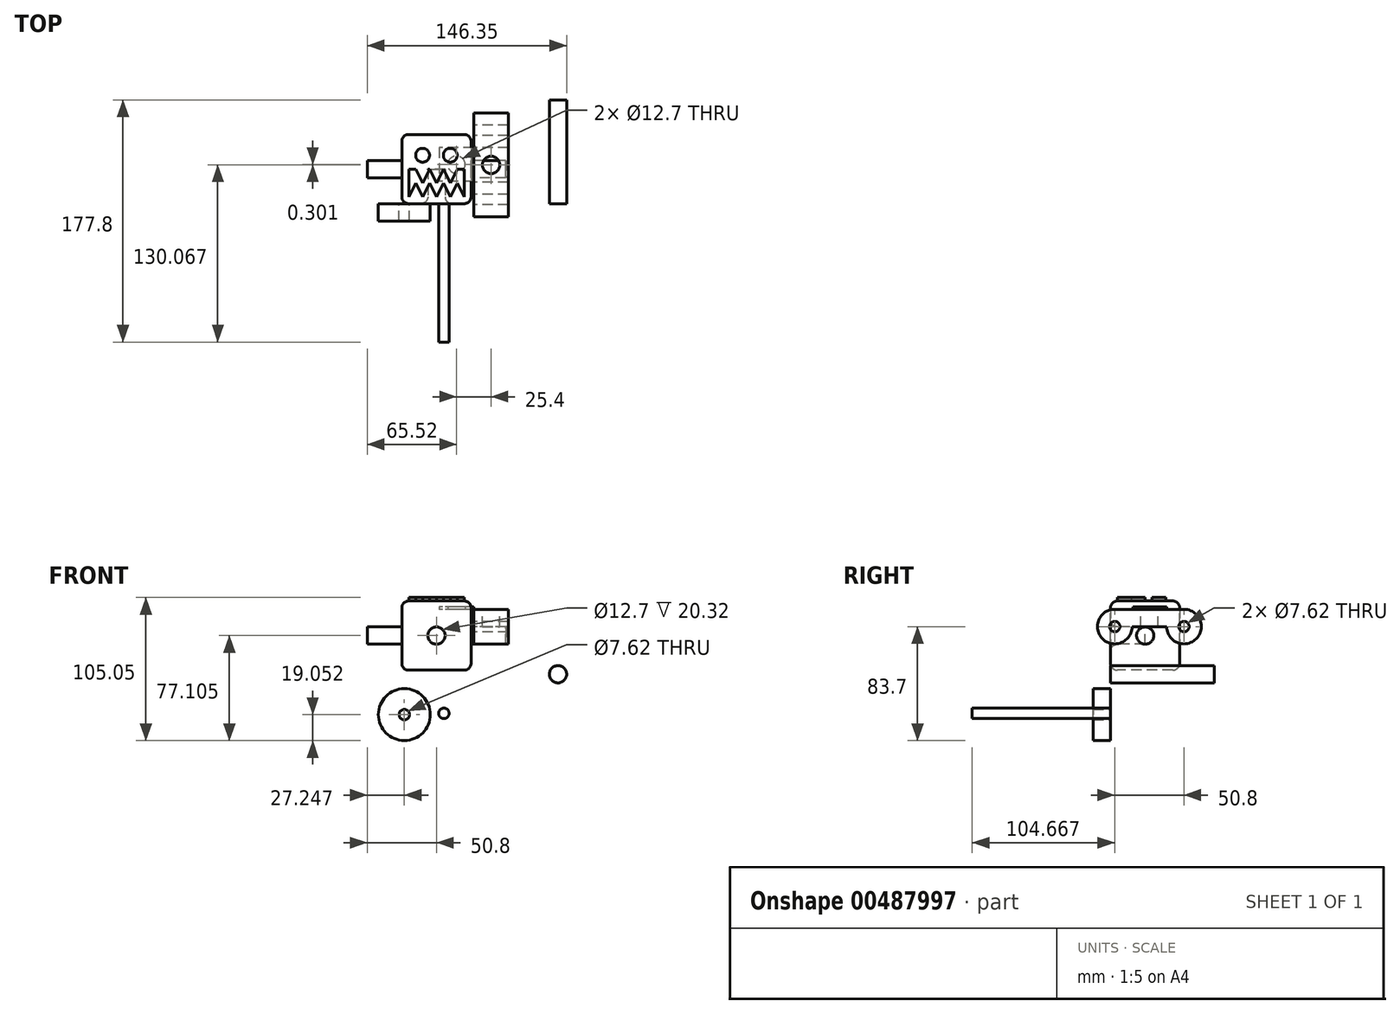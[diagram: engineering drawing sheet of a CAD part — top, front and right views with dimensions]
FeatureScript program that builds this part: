
annotation { "Feature Type Name" : "Feature", "Feature Type Description" : "" }
export const myFeature = defineFeature(function(context is Context, id is Id, definition is map)
    precondition{}
    {
        {
            var Q0;
            Q0=qCreatedBy(makeId("Front.planeOp"),FACE);
            var sketch = newSketch(context, id + "F0", { "sketchPlane" : qUnion([Q0])});
            skCircle(sketch, "E0", {"center": v(-50.97, -29.67) * mm, "radius": 19.05 * mm});
            skCircle(sketch, "E1", {"center": v(-50.97, -29.67) * mm, "radius": 3.81 * mm});
            skSolve(sketch);
        }
        {
            var Q0;
            Q0 = qSketchRegion(id + "F0", true);
            extrude(context, id + "F1", {"entities" : qUnion([Q0]), "depth" : 12.7 * mm, "offsetDistance" : 25.4 * mm});
        }
        {
            var Q0;
            Q0=qCreatedBy(makeId("Front.planeOp"),FACE);
            var sketch = newSketch(context, id + "F2", { "sketchPlane" : qUnion([Q0])});
            skCircle(sketch, "E2", {"center": v(-21.94, -28.72) * mm, "radius": 3.81 * mm});
            skSolve(sketch);
        }
        {
            var Q0;
            Q0 = qSketchRegion(id + "F2", true);
            extrude(context, id + "F3", {"entities" : qUnion([Q0]), "depth" : 101.6 * mm, "offsetDistance" : 25.4 * mm});
        }
        {
            var Q0;
            Q0=qCreatedBy(makeId("Right.planeOp"),FACE);
            var sketch = newSketch(context, id + "F4", { "sketchPlane" : qUnion([Q0])});
            skCircle(sketch, "E3", {"center": v(53.87, 34.98) * mm, "radius": 12.7 * mm});
            skCircle(sketch, "E4", {"center": v(53.87, 34.98) * mm, "radius": 3.81 * mm});
            skLineSegment(sketch, "E5", {"start": v(41.17, 34.98) * mm, "end": v(15.77, 34.98) * mm});
            skCircle(sketch, "E6", {"center": v(3.07, 34.98) * mm, "radius": 12.7 * mm});
            skCircle(sketch, "E7", {"center": v(3.07, 34.98) * mm, "radius": 3.81 * mm});
            skLineSegment(sketch, "E8", {"start": v(53.87, 47.68) * mm, "end": v(3.07, 47.68) * mm});
            skLineSegment(sketch, "E9", {"start": v(53.87, 22.28) * mm, "end": v(3.07, 22.28) * mm});
            skSolve(sketch);
        }
        {
            var Q0;
            Q0=makeQuery(id+"F4.imprint","IMPRINT",FACE,{"disambiguationData":[TD([[makeQuery(id+"F4.imprint","IMPRINT",EDGE,{"derivedFrom":sQuery(id+"F4.wireOp",EDGE,"E4")}),-1.0]])]});
            var Q1;
            Q1=makeQuery(id+"F4.imprint","IMPRINT",FACE,{"disambiguationData":[TD([[makeQuery(id+"F4.imprint","IMPRINT",EDGE,{"derivedFrom":sQuery(id+"F4.wireOp",EDGE,"E7")}),-1.0]])]});
            var Q2;
            {var subQ0=sQuery(id+"F4.wireOp",EDGE,"E5");Q2=makeQuery(id+"F4.imprint","IMPRINT",FACE,{"disambiguationData":[TD([[makeQuery(id+"F4.imprint","IMPRINT",EDGE,{"derivedFrom":subQ0}),-1.0]])]});}
            extrude(context, id + "F5", {"entities" : qUnion([Q0, Q1, Q2]), "depth" : 25.4 * mm, "offsetDistance" : 25.4 * mm});
        }
        {
            var Q0;
            Q0=makeQuery(id+"F5.opExtrude","SWEPT_FACE",FACE,{"disambiguationData":[OSD([sQuery(id+"F4.wireOp",EDGE,"E8")])]});
            var sketch = newSketch(context, id + "F6", { "sketchPlane" : qUnion([Q0])});
            skCircle(sketch, "E10", {"center": v(12.7, 28.47) * mm, "radius": 6.35 * mm});
            skPoint(sketch, "E10.centerSnap0", {"position": v(0, 28.47) * mm});
            skPoint(sketch, "E10.centerSnap1", {"position": v(12.7, 53.87) * mm});
            skSolve(sketch);
        }
        {
            var Q0;
            Q0 = qSketchRegion(id + "F6", true);
            extrude(context, id + "F7", {"entities" : qUnion([Q0]), "operationType" : NewBodyOperationType.REMOVE, "endBound" : BoundingType.THROUGH_ALL, "oppositeDirection" : true, "depth" : 25.4 * mm, "offsetDistance" : 25.4 * mm});
        }
        {
            var Q0;
            Q0=qCreatedBy(makeId("Top.planeOp"),FACE);
            var sketch = newSketch(context, id + "F8", { "sketchPlane" : qUnion([Q0])});
            skLineSegment(sketch, "E11", {"start": v(68.13, 76.2) * mm, "end": v(68.13, 0) * mm});
            skLineSegment(sketch, "E12", {"start": v(68.13, 76.2) * mm, "end": v(61.78, 76.2) * mm});
            skLineSegment(sketch, "E13", {"start": v(61.78, 76.2) * mm, "end": v(61.78, 0) * mm});
            skLineSegment(sketch, "E14", {"start": v(68.13, 0) * mm, "end": v(61.78, 0) * mm});
            skSolve(sketch);
        }
        {
            var Q0;
            Q0=makeQuery(id+"F8.imprint","IMPRINT",FACE,{"disambiguationData":[TD([[makeQuery(id+"F8.imprint","IMPRINT",EDGE,{"derivedFrom":sQuery(id+"F8.wireOp",EDGE,"E11")}),-1.0]])]});
            var Q1;
            Q1=sQuery(id+"F8.wireOp",EDGE,"E13");
            revolve(context, id + "F9", {"surfaceOperationType" : NewSurfaceOperationType.NEW, "entities" : qUnion([Q0]), "axis" : qUnion([Q1]), "revolveType" : RevolveType.FULL});
        }
        {
            var Q0;
            Q0=makeQuery(id+"F5.opExtrude","SWEPT_FACE",FACE,{"disambiguationData":[OSD([sQuery(id+"F4.wireOp",EDGE,"E8")])]});
            var sketch = newSketch(context, id + "F10", { "sketchPlane" : qUnion([Q0])});
            skLineSegment(sketch, "E15", {"start": v(0, 41.2) * mm, "end": v(0, 16.34) * mm});
            skLineSegment(sketch, "E16.MirrorCS", {"start": v(0, 41.2) * mm, "end": v(-25.4, 41.2) * mm});
            skLineSegment(sketch, "E17.MirrorCS", {"start": v(-25.4, 41.2) * mm, "end": v(-25.4, 16.34) * mm});
            skLineSegment(sketch, "E18.MirrorCS", {"start": v(0, 16.34) * mm, "end": v(-25.4, 16.34) * mm});
            skCircle(sketch, "E19", {"center": v(-12.7, 28.77) * mm, "radius": 6.35 * mm});
            skSolve(sketch);
        }
        {
            var Q0;
            Q0=makeQuery(id+"F10.imprint","IMPRINT",FACE,{"disambiguationData":[TD([[makeQuery(id+"F10.imprint","IMPRINT",EDGE,{"derivedFrom":sQuery(id+"F10.wireOp",EDGE,"E16.MirrorCS")}),1.0]])]});
            extrude(context, id + "F11", {"entities" : qUnion([Q0]), "depth" : 1.9 * mm, "offsetDistance" : 25.4 * mm});
        }
        {
            var Q0;
            Q0=qCreatedBy(makeId("Front.planeOp"),FACE);
            var sketch = newSketch(context, id + "F12", { "sketchPlane" : qUnion([Q0])});
            skLineSegment(sketch, "E20", {"start": v(-52.82, 53.79) * mm, "end": v(-52.82, 2.99) * mm});
            skLineSegment(sketch, "E21", {"start": v(-52.82, 2.99) * mm, "end": v(-2.02, 2.99) * mm});
            skLineSegment(sketch, "E22", {"start": v(-2.02, 2.99) * mm, "end": v(-2.02, 53.79) * mm});
            skLineSegment(sketch, "E23", {"start": v(-2.02, 53.79) * mm, "end": v(-52.82, 53.79) * mm});
            skCircle(sketch, "E24", {"center": v(-27.42, 28.39) * mm, "radius": 6.35 * mm});
            skPoint(sketch, "E24.centerSnap0", {"position": v(-27.42, 53.79) * mm});
            skPoint(sketch, "E24.centerSnap1", {"position": v(-52.82, 28.39) * mm});
            skSolve(sketch);
        }
        {
            var Q0;
            Q0=makeQuery(id+"F12.imprint","IMPRINT",FACE,{"disambiguationData":[TD([[makeQuery(id+"F12.imprint","IMPRINT",EDGE,{"derivedFrom":sQuery(id+"F12.wireOp",EDGE,"E20")}),1.0]])]});
            var Q1;
            Q1=makeQuery(id+"F12.imprint","IMPRINT",FACE,{"disambiguationData":[TD([[makeQuery(id+"F12.imprint","IMPRINT",EDGE,{"derivedFrom":sQuery(id+"F12.wireOp",EDGE,"E24")}),1.0]])]});
            extrude(context, id + "F13", {"entities" : qUnion([Q0, Q1]), "oppositeDirection" : true, "depth" : 50.8 * mm, "offsetDistance" : 25.4 * mm});
        }
        {
            var Q0;
            Q0=makeQuery(id+"F13.opExtrude","CAP_FACE",FACE,{"disambiguationData":[OSD([sQuery(id+"F12.wireOp",EDGE,"E20"),sQuery(id+"F12.wireOp",EDGE,"E21"),sQuery(id+"F12.wireOp",EDGE,"E22"),sQuery(id+"F12.wireOp",EDGE,"E23")])],"isStart":true});
            var sketch = newSketch(context, id + "F14", { "sketchPlane" : qUnion([Q0])});
            skCircle(sketch, "E25", {"center": v(-27.42, 28.39) * mm, "radius": 6.35 * mm});
            skSolve(sketch);
        }
        {
            var Q0;
            Q0=makeQuery(id+"F14.imprint","IMPRINT",FACE,{"disambiguationData":[TD([[makeQuery(id+"F14.imprint","IMPRINT",EDGE,{"derivedFrom":sQuery(id+"F14.wireOp",EDGE,"E25")}),1.0]])]});
            extrude(context, id + "F15", {"entities" : qUnion([Q0]), "operationType" : NewBodyOperationType.REMOVE, "oppositeDirection" : true, "depth" : 25.4 * mm, "offsetDistance" : 25.4 * mm});
        }
        {
            var Q0;
            Q0=makeQuery(id+"F13.opExtrude","CAP_EDGE",EDGE,{"disambiguationData":[OSD([sQuery(id+"F12.wireOp",EDGE,"E23")])],"isStart":true});
            var Q1;
            Q1=makeQuery(id+"F13.opExtrude","SWEPT_EDGE",EDGE,{"disambiguationData":[OSD([sQuery(id+"F12.wireOp",EDGE,"E20"),sQuery(id+"F12.wireOp",EDGE,"E23")])]});
            var Q2;
            Q2=makeQuery(id+"F13.opExtrude","CAP_EDGE",EDGE,{"disambiguationData":[OSD([sQuery(id+"F12.wireOp",EDGE,"E20")])],"isStart":true});
            var Q3;
            Q3=makeQuery(id+"F13.opExtrude","SWEPT_EDGE",EDGE,{"disambiguationData":[OSD([sQuery(id+"F12.wireOp",EDGE,"E20"),sQuery(id+"F12.wireOp",EDGE,"E21")])]});
            var Q4;
            Q4=makeQuery(id+"F13.opExtrude","CAP_EDGE",EDGE,{"disambiguationData":[OSD([sQuery(id+"F12.wireOp",EDGE,"E21")])],"isStart":true});
            var Q5;
            Q5=makeQuery(id+"F13.opExtrude","CAP_FACE",FACE,{"disambiguationData":[OSD([sQuery(id+"F12.wireOp",EDGE,"E20"),sQuery(id+"F12.wireOp",EDGE,"E21"),sQuery(id+"F12.wireOp",EDGE,"E22"),sQuery(id+"F12.wireOp",EDGE,"E23")])],"isStart":true});
            var Q6;
            Q6=makeQuery(id+"F13.opExtrude","SWEPT_EDGE",EDGE,{"disambiguationData":[OSD([sQuery(id+"F12.wireOp",EDGE,"E21"),sQuery(id+"F12.wireOp",EDGE,"E22")])]});
            var Q7;
            Q7=makeQuery(id+"F13.opExtrude","CAP_EDGE",EDGE,{"disambiguationData":[OSD([sQuery(id+"F12.wireOp",EDGE,"E23")])],"isStart":false});
            var Q8;
            Q8=makeQuery(id+"F13.opExtrude","SWEPT_EDGE",EDGE,{"disambiguationData":[OSD([sQuery(id+"F12.wireOp",EDGE,"E22"),sQuery(id+"F12.wireOp",EDGE,"E23")])]});
            var Q9;
            Q9=makeQuery(id+"F13.opExtrude","CAP_EDGE",EDGE,{"disambiguationData":[OSD([sQuery(id+"F12.wireOp",EDGE,"E22")])],"isStart":false});
            var Q10;
            Q10=makeQuery(id+"F13.opExtrude","CAP_EDGE",EDGE,{"disambiguationData":[OSD([sQuery(id+"F12.wireOp",EDGE,"E20")])],"isStart":false});
            var Q11;
            Q11=makeQuery(id+"F13.opExtrude","CAP_EDGE",EDGE,{"disambiguationData":[OSD([sQuery(id+"F12.wireOp",EDGE,"E21")])],"isStart":false});
            fillet(context, id + "F16", {"entities" : qUnion([Q0, Q1, Q2, Q3, Q4, Q5, Q6, Q7, Q8, Q9, Q10, Q11]), "radius" : 5.08 * mm, "tangentPropagation" : true, "allowEdgeOverflow" : false});
        }
        {
            var Q0;
            Q0=makeQuery(id+"F13.opExtrude","SWEPT_FACE",FACE,{"disambiguationData":[OSD([sQuery(id+"F12.wireOp",EDGE,"E20")])]});
            var sketch = newSketch(context, id + "F17", { "sketchPlane" : qUnion([Q0])});
            skCircle(sketch, "E26", {"center": v(-25.4, 28.39) * mm, "radius": 6.35 * mm});
            skPoint(sketch, "E26.centerSnap0", {"position": v(-5.08, 28.39) * mm});
            skPoint(sketch, "E26.centerSnap1", {"position": v(-25.4, 48.7) * mm});
            skSolve(sketch);
        }
        {
            var Q0;
            Q0=makeQuery(id+"F17.imprint","IMPRINT",FACE,{"disambiguationData":[TD([[makeQuery(id+"F17.imprint","IMPRINT",EDGE,{"derivedFrom":sQuery(id+"F17.wireOp",EDGE,"E26")}),1.0]])]});
            extrude(context, id + "F18", {"entities" : qUnion([Q0]), "operationType" : NewBodyOperationType.ADD, "depth" : 25.4 * mm, "offsetDistance" : 25.4 * mm});
        }
        {
            var Q0;
            Q0=makeQuery(id+"F13.opExtrude","SWEPT_FACE",FACE,{"disambiguationData":[OSD([sQuery(id+"F12.wireOp",EDGE,"E22")])]});
            var sketch = newSketch(context, id + "F19", { "sketchPlane" : qUnion([Q0])});
            skCircle(sketch, "E27", {"center": v(25.4, 28.39) * mm, "radius": 6.35 * mm});
            skPoint(sketch, "E27.centerSnap0", {"position": v(5.08, 28.39) * mm});
            skPoint(sketch, "E27.centerSnap1", {"position": v(25.4, 48.7) * mm});
            skSolve(sketch);
        }
        {
            var Q0;
            Q0 = qSketchRegion(id + "F19", true);
            extrude(context, id + "F20", {"entities" : qUnion([Q0]), "operationType" : NewBodyOperationType.ADD, "depth" : 25.4 * mm, "offsetDistance" : 25.4 * mm});
        }
        {
            var Q0;
            Q0=makeQuery(id+"F13.opExtrude","SWEPT_FACE",FACE,{"disambiguationData":[OSD([sQuery(id+"F12.wireOp",EDGE,"E23")])]});
            var sketch = newSketch(context, id + "F21", { "sketchPlane" : qUnion([Q0])});
            skCircle(sketch, "E28", {"center": v(-37.58, 35.56) * mm, "radius": 5.08 * mm});
            skCircle(sketch, "E29", {"center": v(-17.26, 35.56) * mm, "radius": 5.08 * mm});
            skLineSegment(sketch, "E30.left", {"start": v(-47.74, 25.4) * mm, "end": v(-47.74, 5.08) * mm});
            skLineSegment(sketch, "E30.right", {"start": v(-7.1, 25.4) * mm, "end": v(-7.1, 5.08) * mm});
            skLineSegment(sketch, "E31", {"start": v(-47.74, 5.08) * mm, "end": v(-37.58, 5.08) * mm});
            skLineSegment(sketch, "E32", {"start": v(-42.66, 15.24) * mm, "end": v(-47.74, 5.08) * mm});
            skLineSegment(sketch, "E33", {"start": v(-42.66, 15.24) * mm, "end": v(-37.58, 5.08) * mm});
            skLineSegment(sketch, "E34", {"start": v(-37.58, 5.08) * mm, "end": v(-32.5, 15.24) * mm});
            skLineSegment(sketch, "E35", {"start": v(-32.5, 15.24) * mm, "end": v(-27.42, 5.08) * mm});
            skLineSegment(sketch, "E36", {"start": v(-27.42, 5.08) * mm, "end": v(-22.34, 15.24) * mm});
            skLineSegment(sketch, "E37", {"start": v(-22.34, 15.24) * mm, "end": v(-17.26, 5.08) * mm});
            skLineSegment(sketch, "E38", {"start": v(-17.26, 5.08) * mm, "end": v(-12.18, 15.24) * mm});
            skLineSegment(sketch, "E39", {"start": v(-47.74, 25.4) * mm, "end": v(-37.58, 25.4) * mm});
            skLineSegment(sketch, "E40", {"start": v(-37.58, 25.4) * mm, "end": v(-27.42, 25.4) * mm});
            skLineSegment(sketch, "E41", {"start": v(-27.42, 25.4) * mm, "end": v(-17.26, 25.4) * mm});
            skLineSegment(sketch, "E42", {"start": v(-17.26, 25.4) * mm, "end": v(-7.1, 25.4) * mm});
            skLineSegment(sketch, "E43", {"start": v(-42.66, 25.4) * mm, "end": v(-37.58, 15.24) * mm});
            skLineSegment(sketch, "E44", {"start": v(-32.5, 25.4) * mm, "end": v(-37.58, 15.24) * mm});
            skLineSegment(sketch, "E45", {"start": v(-32.5, 25.4) * mm, "end": v(-27.42, 15.24) * mm});
            skLineSegment(sketch, "E46", {"start": v(-22.34, 25.4) * mm, "end": v(-27.42, 15.24) * mm});
            skLineSegment(sketch, "E47", {"start": v(-22.34, 25.4) * mm, "end": v(-17.26, 15.24) * mm});
            skLineSegment(sketch, "E48", {"start": v(-17.26, 15.24) * mm, "end": v(-12.18, 25.4) * mm});
            skLineSegment(sketch, "E49", {"start": v(-12.18, 15.24) * mm, "end": v(-7.1, 5.08) * mm});
            skSolve(sketch);
        }
        {
            var Q0;
            Q0=makeQuery(id+"F21.imprint","IMPRINT",FACE,{"disambiguationData":[TD([[makeQuery(id+"F21.imprint","IMPRINT",EDGE,{"derivedFrom":sQuery(id+"F21.wireOp",EDGE,"E28")}),1.0]])]});
            var Q1;
            Q1=makeQuery(id+"F21.imprint","IMPRINT",FACE,{"disambiguationData":[TD([[makeQuery(id+"F21.imprint","IMPRINT",EDGE,{"derivedFrom":sQuery(id+"F21.wireOp",EDGE,"E29")}),1.0]])]});
            var Q2;
            {var subQ1=sQuery(id+"F21.wireOp",EDGE,"E30.left");Q2=makeQuery(id+"F21.imprint","IMPRINT",FACE,{"disambiguationData":[TD([[makeQuery(id+"F21.imprint","IMPRINT",EDGE,{"derivedFrom":subQ1}),1.0]])]});}
            extrude(context, id + "F22", {"entities" : qUnion([Q0, Q1, Q2]), "operationType" : NewBodyOperationType.ADD, "depth" : 2.54 * mm, "offsetDistance" : 25.4 * mm});
        }
    });
